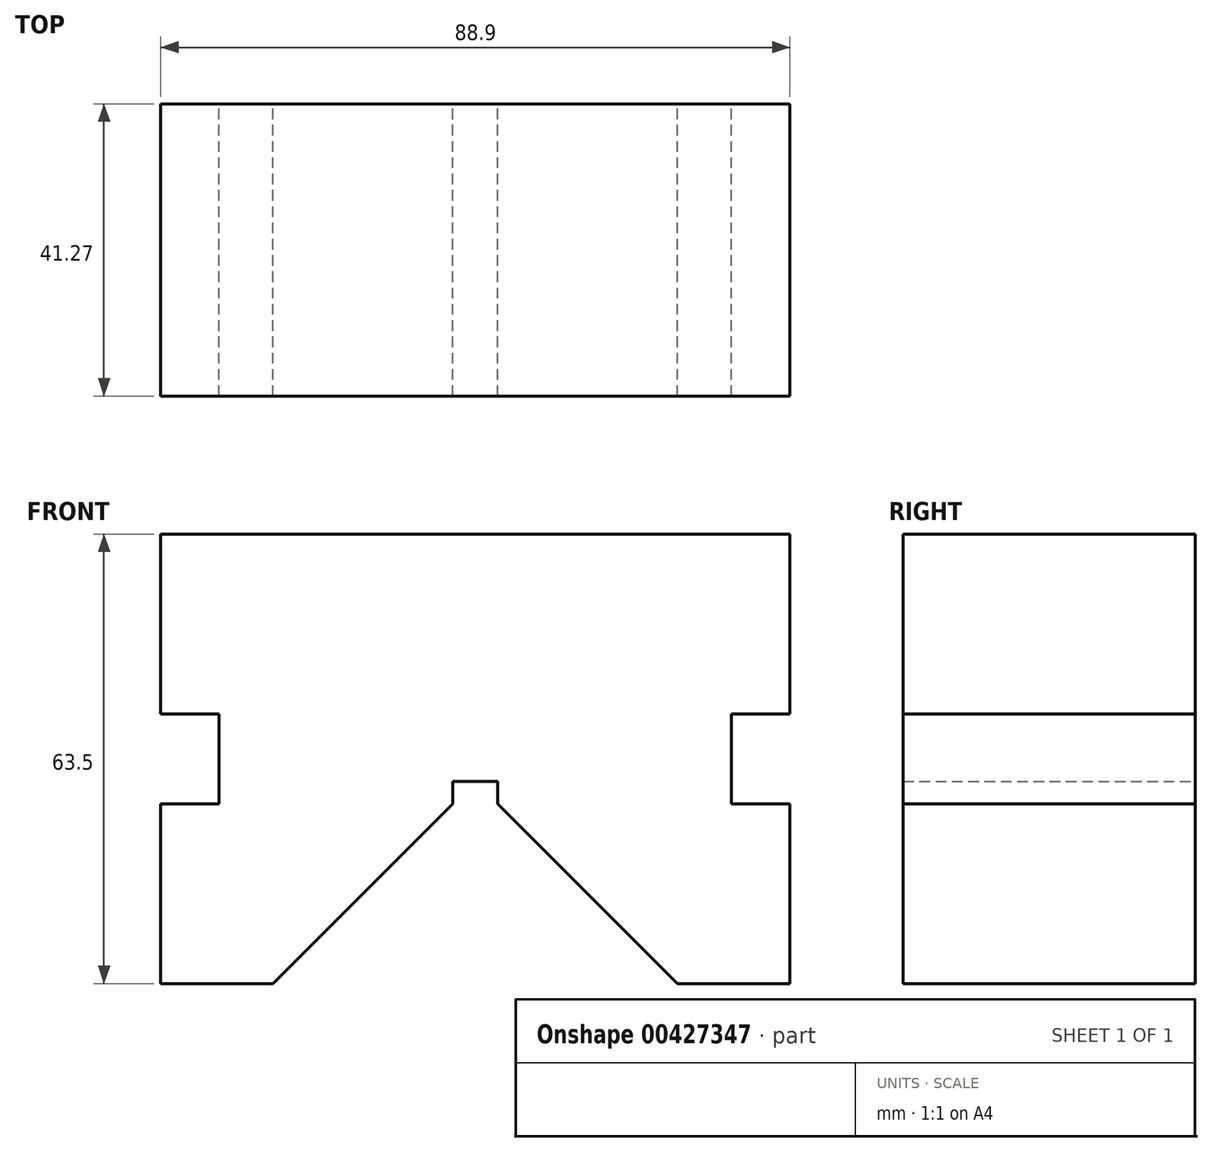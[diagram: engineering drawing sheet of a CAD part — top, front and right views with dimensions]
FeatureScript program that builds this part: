
annotation { "Feature Type Name" : "Feature", "Feature Type Description" : "" }
export const myFeature = defineFeature(function(context is Context, id is Id, definition is map)
    precondition{}
    {
        {
            var Q0;
            Q0=qCreatedBy(makeId("Front.planeOp"),FACE);
            var sketch = newSketch(context, id + "F0", { "sketchPlane" : qUnion([Q0])});
            skLineSegment(sketch, "E0.bottom", {"start": v(0, 0) * mm, "end": v(15.88, 0) * mm});
            skLineSegment(sketch, "E0.top", {"start": v(0, 63.5) * mm, "end": v(88.9, 63.5) * mm});
            skLineSegment(sketch, "E0.left", {"start": v(0, 0) * mm, "end": v(0, 25.4) * mm});
            skLineSegment(sketch, "E0.right", {"start": v(88.9, 0) * mm, "end": v(88.9, 25.4) * mm});
            skLineSegment(sketch, "E1.bottom", {"start": v(0, 38.1) * mm, "end": v(8.25, 38.1) * mm});
            skLineSegment(sketch, "E1.top", {"start": v(0, 25.4) * mm, "end": v(8.25, 25.4) * mm});
            skLineSegment(sketch, "E1.right", {"start": v(8.25, 38.1) * mm, "end": v(8.25, 25.4) * mm});
            skLineSegment(sketch, "E2.bottom", {"start": v(88.9, 38.1) * mm, "end": v(80.65, 38.1) * mm});
            skLineSegment(sketch, "E2.top", {"start": v(88.9, 25.4) * mm, "end": v(80.65, 25.4) * mm});
            skLineSegment(sketch, "E2.right", {"start": v(80.65, 38.1) * mm, "end": v(80.65, 25.4) * mm});
            skLineSegment(sketch, "E3.trimOffspring", {"start": v(88.9, 38.1) * mm, "end": v(88.9, 63.5) * mm});
            skLineSegment(sketch, "E4.trimOffspring", {"start": v(0, 38.1) * mm, "end": v(0, 63.5) * mm});
            skPoint(sketch, "E5", {"position": v(15.88, 0) * mm});
            skPoint(sketch, "E6", {"position": v(73.03, 0) * mm});
            skLineSegment(sketch, "E7", {"start": v(73.03, 0) * mm, "end": v(47.62, 25.4) * mm});
            skLineSegment(sketch, "E8", {"start": v(15.87, 0) * mm, "end": v(41.28, 25.4) * mm});
            skLineSegment(sketch, "E9", {"start": v(41.28, 25.4) * mm, "end": v(41.28, 28.58) * mm});
            skLineSegment(sketch, "E10", {"start": v(41.28, 28.58) * mm, "end": v(47.63, 28.58) * mm});
            skLineSegment(sketch, "E11", {"start": v(47.62, 28.58) * mm, "end": v(47.62, 25.4) * mm});
            skLineSegment(sketch, "E12.trimOffspring", {"start": v(73.02, 0) * mm, "end": v(88.9, 0) * mm});
            skSolve(sketch);
        }
        {
            var Q0;
            Q0 = qSketchRegion(id + "F0", true);
            extrude(context, id + "F1", {"entities" : qUnion([Q0]), "depth" : 41.27 * mm});
        }
    });
